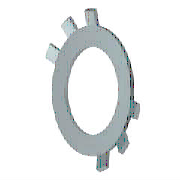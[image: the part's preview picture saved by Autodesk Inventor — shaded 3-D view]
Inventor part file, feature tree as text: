
AUTODESK INVENTOR PART (.ipt)
format: ipt  version: 2020 (Build 240168000, 168)  size: 227,840 bytes
history: native  units: mm (DEFAULTED — no unit token found)
features: extrude x3, other x2, sketch x2, plane x1
ambient origin geometry x8: Origin, YZ Plane, XZ Plane, XY Plane, X Axis, Y Axis, Z Axis, Center Point
bodies: Solid1 (feature_tree)
feature tree (8):
  other  "轴承体"
  sketch  "草图2"  dims[d3=40.0mm d4=52.0mm d5=4.363323mm d6=1.0mm d7=90.0deg d8=30.5mm d9=4.8mm d17=1.0mm d12=0.0mm d13=1.0mm d14=0.0mm d18=0.0mm d20=0.0mm d21=1.0mm d23=5.0mm d24=0.0mm d25=27.0mm d32=4.8mm d34=4.8mm d36=30.0deg d38=2.4mm d39=30.0deg d40=15.0deg d41=4.8mm d42=30.0deg d43=30.0deg d45=4.8mm d47=4.8mm d49=90.0deg d50=0.0mm]
  extrude  "切口"  Depth=1.0mm
  extrude  "榫1"  Depth=4.8mm
  extrude  "榫2"  Depth=4.8mm
  other  "Work Axis1"
  plane  "Work Plane1"
  sketch  "草图1"  dims[d1=1.0mm d2=30.5mm]
